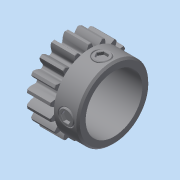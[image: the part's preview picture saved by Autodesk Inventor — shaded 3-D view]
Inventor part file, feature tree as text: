
AUTODESK INVENTOR PART (.ipt)
format: ipt  version: 2015 (Build 190159000, 159)  size: 1,058,304 bytes
history: native  units: in
note: dims shown in document units (in); Inventor stores cm internally (conversion verified against a paired STEP export)
features: imported_body x3, other x1, extrude x1, sketch x1
ambient origin geometry x8: Origin, YZ Plane, XZ Plane, XY Plane, X Axis, Y Axis, Z Axis, Center Point
bodies: Solid1 (feature_tree), Solid2 (feature_tree), Solid3 (feature_tree)
feature tree (6):
  other  "s10a9z-024h0181"
  extrude  "Extrusion1"  TaperAngle=0.0deg  [1 undecoded]
  imported_body  "Base1"
  imported_body  "Base2"
  imported_body  "Base3"
  sketch  "Sketch1"  dims[d0=0.5906in d1=0.0in d2=0.0in]
note: 1 required parameter value undecoded (feature->parameter linkage not recoverable at this tier; creation-order binding heuristic only, values carry confidence <= 0.55)
